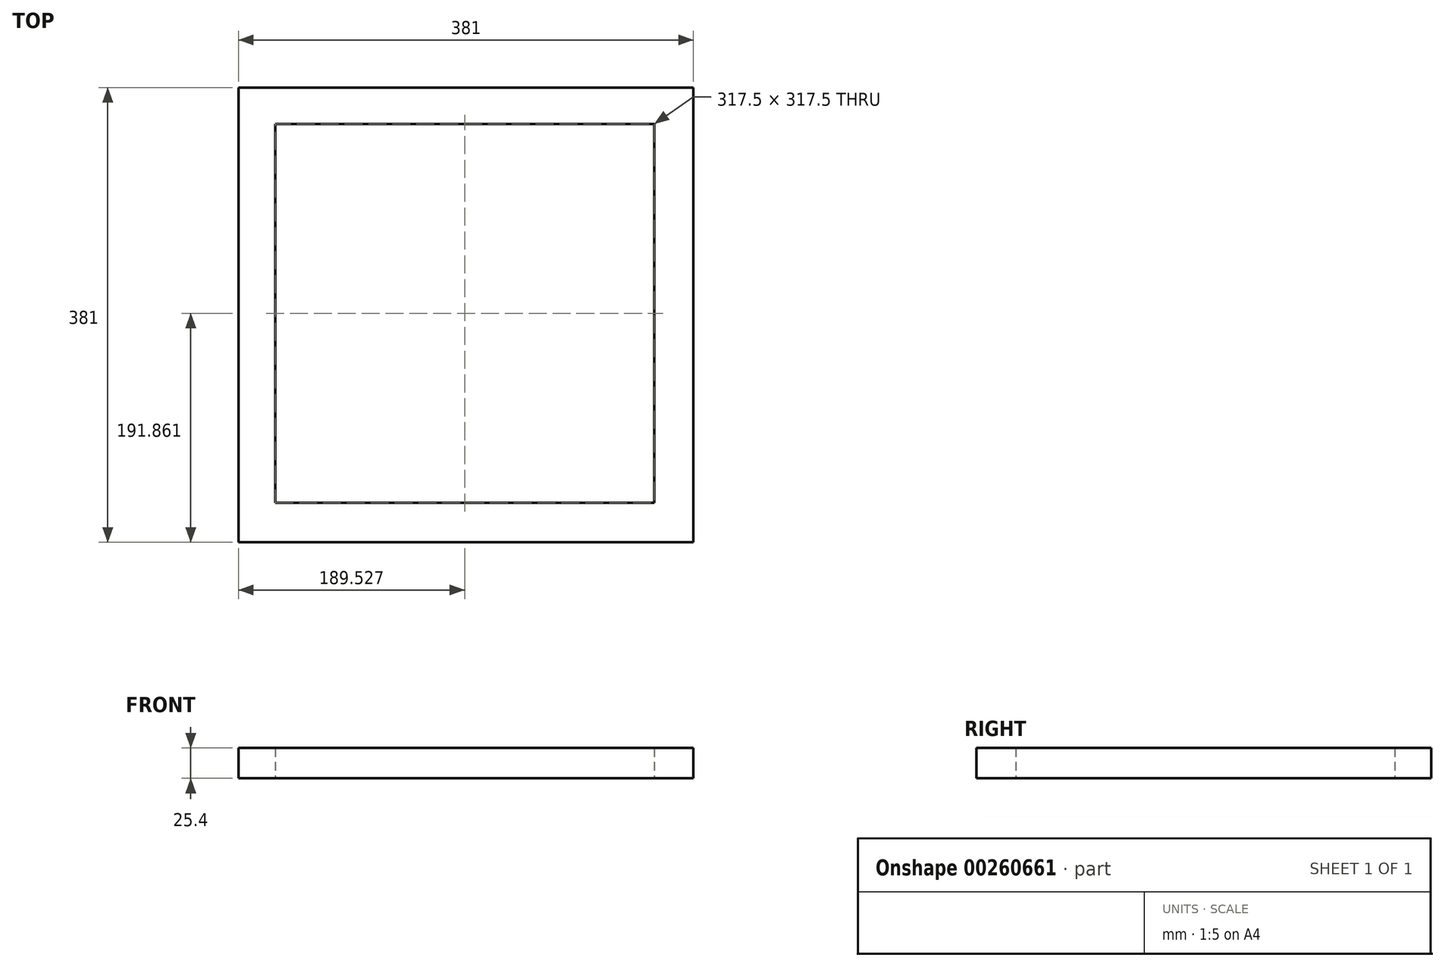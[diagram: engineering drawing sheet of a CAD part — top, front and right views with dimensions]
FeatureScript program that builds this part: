
annotation { "Feature Type Name" : "Feature", "Feature Type Description" : "" }
export const myFeature = defineFeature(function(context is Context, id is Id, definition is map)
    precondition{}
    {
        {
            var Q0;
            Q0=qCreatedBy(makeId("Top.planeOp"),FACE);
            var sketch = newSketch(context, id + "F0", { "sketchPlane" : qUnion([Q0])});
            skLineSegment(sketch, "E0.bottom", {"start": v(-183.93, 186.5) * mm, "end": v(197.07, 186.5) * mm});
            skLineSegment(sketch, "E0.top", {"start": v(-183.93, -194.5) * mm, "end": v(197.07, -194.5) * mm});
            skLineSegment(sketch, "E0.left", {"start": v(-183.93, 186.5) * mm, "end": v(-183.93, -194.5) * mm});
            skLineSegment(sketch, "E0.right", {"start": v(197.07, 186.5) * mm, "end": v(197.07, -194.5) * mm});
            skLineSegment(sketch, "E1.bottom", {"start": v(-153.15, 156.11) * mm, "end": v(164.35, 156.11) * mm});
            skLineSegment(sketch, "E1.top", {"start": v(-153.15, -161.39) * mm, "end": v(164.35, -161.39) * mm});
            skLineSegment(sketch, "E1.left", {"start": v(-153.15, 156.11) * mm, "end": v(-153.15, -161.39) * mm});
            skLineSegment(sketch, "E1.right", {"start": v(164.35, 156.11) * mm, "end": v(164.35, -161.39) * mm});
            skSolve(sketch);
        }
        {
            var Q0;
            Q0 = qSketchRegion(id + "F0", true);
            extrude(context, id + "F1", {"entities" : qUnion([Q0]), "depth" : 25.4 * mm});
        }
    });
